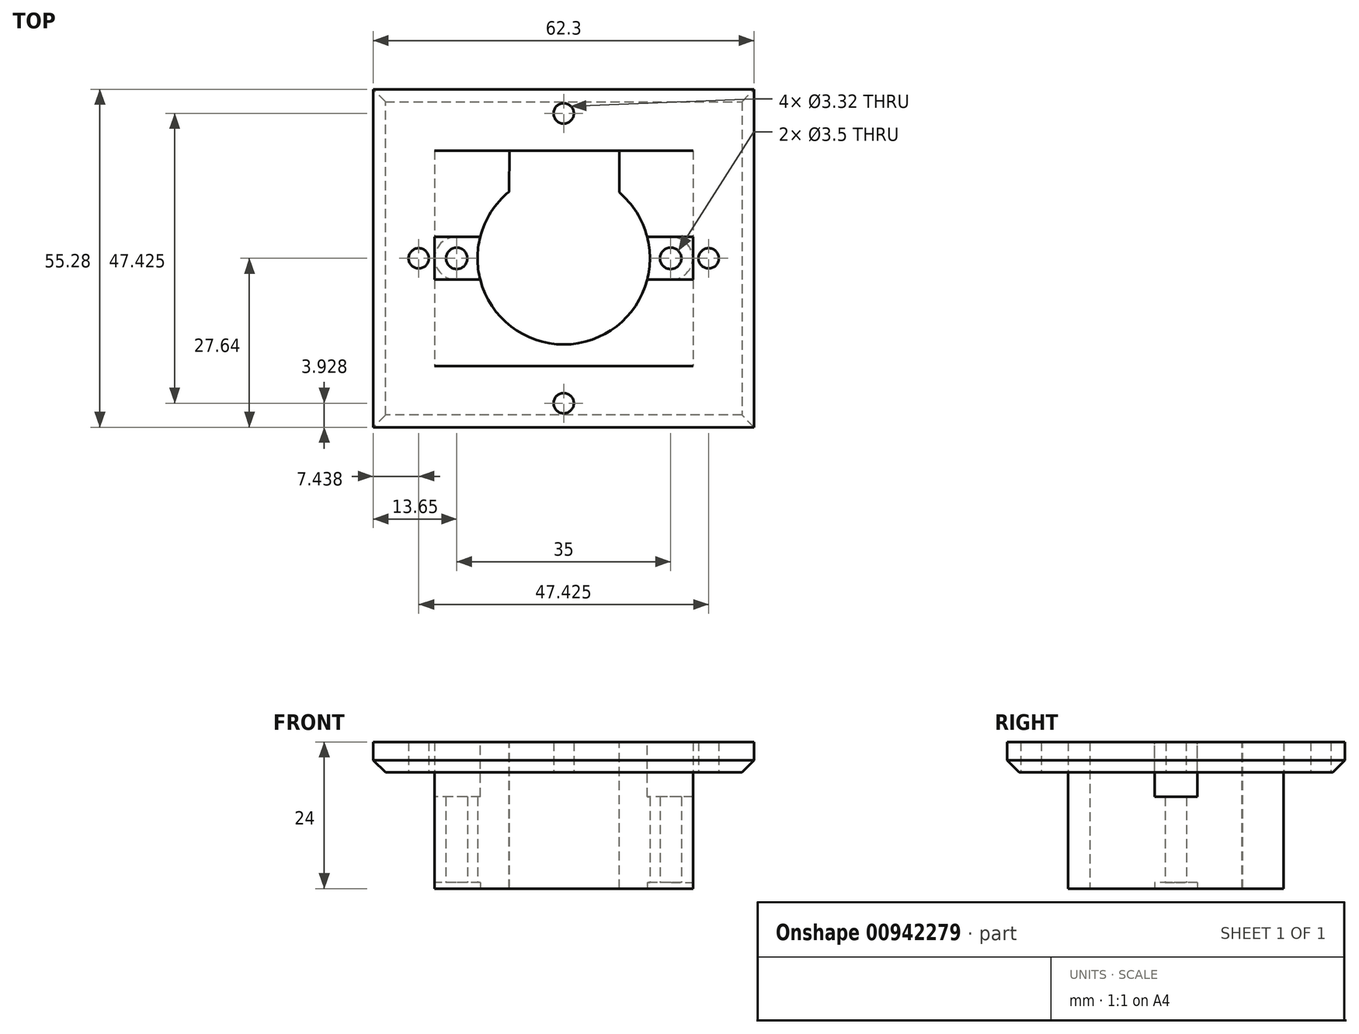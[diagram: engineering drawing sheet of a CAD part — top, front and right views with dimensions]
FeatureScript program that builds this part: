
annotation { "Feature Type Name" : "Feature", "Feature Type Description" : "" }
export const myFeature = defineFeature(function(context is Context, id is Id, definition is map)
    precondition{}
    {
        {
            var Q0;
            Q0=qCreatedBy(makeId("Top.planeOp"),FACE);
            var sketch = newSketch(context, id + "F0", { "sketchPlane" : qUnion([Q0])});
            skCircle(sketch, "E0", {"center": v(0, 0) * mm, "radius": 14.1 * mm});
            skLineSegment(sketch, "E1.bottom", {"start": v(17.6, 3.5) * mm, "end": v(13.66, 3.5) * mm});
            skLineSegment(sketch, "E1.top", {"start": v(17.6, -3.5) * mm, "end": v(13.66, -3.5) * mm});
            skLineSegment(sketch, "E1.left", {"start": v(21.1, 0) * mm, "end": v(21.1, 0) * mm});
            skLineSegment(sketch, "E1.right", {"start": v(-21.1, 0) * mm, "end": v(-21.1, 0) * mm});
            skPoint(sketch, "E2.startSnap0", {"position": v(-21.1, 0) * mm});
            skPoint(sketch, "E2.end.orphan", {"position": v(-21.1, 0) * mm});
            skPoint(sketch, "E2.start.orphan", {"position": v(-14.1, 0) * mm});
            skLineSegment(sketch, "E3.bottom", {"start": v(-17.5, 0) * mm, "end": v(-14.1, 0) * mm});
            skLineSegment(sketch, "E3.top", {"start": v(-17.5, 0) * mm, "end": v(-14.1, 0) * mm});
            skLineSegment(sketch, "E3.left", {"start": v(-17.5, 0) * mm, "end": v(-17.5, 0) * mm});
            skLineSegment(sketch, "E3.right", {"start": v(17.5, 0) * mm, "end": v(17.5, 0) * mm});
            skCircle(sketch, "E4", {"center": v(-17.5, 0) * mm, "radius": 1.75 * mm});
            skCircle(sketch, "E5", {"center": v(17.5, 0) * mm, "radius": 1.75 * mm});
            skLineSegment(sketch, "E6.bottom", {"start": v(21.15, 17.62) * mm, "end": v(-21.15, 17.62) * mm});
            skLineSegment(sketch, "E6.top", {"start": v(21.15, -17.62) * mm, "end": v(-21.15, -17.62) * mm});
            skLineSegment(sketch, "E6.left", {"start": v(21.15, 17.62) * mm, "end": v(21.15, -17.62) * mm});
            skLineSegment(sketch, "E6.right", {"start": v(-21.15, 17.62) * mm, "end": v(-21.15, -17.62) * mm});
            skLineSegment(sketch, "E7.trimOffspring", {"start": v(-13.66, 3.5) * mm, "end": v(-17.6, 3.5) * mm});
            skLineSegment(sketch, "E8.trimOffspring", {"start": v(14.1, 0) * mm, "end": v(17.5, 0) * mm});
            skLineSegment(sketch, "E9.trimOffspring", {"start": v(-13.66, -3.5) * mm, "end": v(-17.6, -3.5) * mm});
            skPoint(sketch, "E10.visualSharp", {"position": v(-21.1, 3.5) * mm});
            skArc(sketch, "E10.filletArc", {"start": v(-17.6, 3.5) * mm, "mid": v(-20.07, 2.47) * mm, "end": v(-21.1, 0) * mm});
            skPoint(sketch, "E11.visualSharp", {"position": v(-21.1, -3.5) * mm});
            skArc(sketch, "E11.filletArc", {"start": v(-21.1, 0) * mm, "mid": v(-20.07, -2.47) * mm, "end": v(-17.6, -3.5) * mm});
            skPoint(sketch, "E12.visualSharp", {"position": v(21.1, -3.5) * mm});
            skArc(sketch, "E12.filletArc", {"start": v(17.6, -3.5) * mm, "mid": v(20.07, -2.47) * mm, "end": v(21.1, 0) * mm});
            skPoint(sketch, "E13.visualSharp", {"position": v(21.1, 3.5) * mm});
            skArc(sketch, "E13.filletArc", {"start": v(21.1, 0) * mm, "mid": v(20.07, 2.47) * mm, "end": v(17.6, 3.5) * mm});
            skSolve(sketch);
        }
        {
            var Q0;
            {var subQ1=sQuery(id+"F0.wireOp",EDGE,"E1.bottom");Q0=makeQuery(id+"F0.imprint","IMPRINT",FACE,{"disambiguationData":[TD([[makeQuery(id+"F0.imprint","IMPRINT",EDGE,{"derivedFrom":subQ1}),-1.0]])]});}
            var Q1;
            {var subQ1=sQuery(id+"F0.wireOp",EDGE,"E1.top");Q1=makeQuery(id+"F0.imprint","IMPRINT",FACE,{"disambiguationData":[TD([[makeQuery(id+"F0.imprint","IMPRINT",EDGE,{"derivedFrom":subQ1}),1.0]])]});}
            var Q2;
            Q2=makeQuery(id+"F0.imprint","IMPRINT",FACE,{"disambiguationData":[TD([[makeQuery(id+"F0.imprint","IMPRINT",EDGE,{"derivedFrom":sQuery(id+"F0.wireOp",EDGE,"E4")}),-1.0]])]});
            var Q3;
            {var subQ1=sQuery(id+"F0.wireOp",EDGE,"E1.bottom");Q3=makeQuery(id+"F0.imprint","IMPRINT",FACE,{"disambiguationData":[TD([[makeQuery(id+"F0.imprint","IMPRINT",EDGE,{"derivedFrom":subQ1}),1.0]])]});}
            extrude(context, id + "F1", {"entities" : qUnion([Q0, Q1, Q2, Q3]), "depth" : 20 * mm, "offsetDistance" : 25 * mm});
        }
        {
            var Q0;
            Q0=makeQuery(id+"F1.opExtrude","CAP_FACE",FACE,{"disambiguationData":[OSD([sQuery(id+"F0.wireOp",EDGE,"E0"),sQuery(id+"F0.wireOp",EDGE,"E4"),sQuery(id+"F0.wireOp",EDGE,"E5"),sQuery(id+"F0.wireOp",EDGE,"E6.bottom"),sQuery(id+"F0.wireOp",EDGE,"E6.top"),sQuery(id+"F0.wireOp",EDGE,"E6.left"),sQuery(id+"F0.wireOp",EDGE,"E6.right")])],"isStart":false});
            var sketch = newSketch(context, id + "F2", { "sketchPlane" : qUnion([Q0])});
            skLineSegment(sketch, "E14.bottom", {"start": v(-8.89, 17.63) * mm, "end": v(9.11, 17.63) * mm});
            skLineSegment(sketch, "E14.left", {"start": v(-8.89, 17.63) * mm, "end": v(-8.93, 10.91) * mm});
            skLineSegment(sketch, "E14.right", {"start": v(9.11, 17.63) * mm, "end": v(9.07, 10.8) * mm});
            skPoint(sketch, "E14.middle", {"position": v(0, 0) * mm});
            skArc(sketch, "E15", {"start": v(9.07, 10.8) * mm, "mid": v(0.1, 14.1) * mm, "end": v(-8.93, 10.91) * mm});
            skPoint(sketch, "E14.top.end.orphan", {"position": v(8.89, -17.63) * mm});
            skPoint(sketch, "E14.top.start.orphan", {"position": v(-9.11, -17.63) * mm});
            skSolve(sketch);
        }
        {
            var Q0;
            {var subQ0=sQuery(id+"F2.wireOp",EDGE,"E15");Q0=makeQuery(id+"F2.imprint","IMPRINT",FACE,{"disambiguationData":[TD([[makeQuery(id+"F2.imprint","IMPRINT",EDGE,{"derivedFrom":subQ0}),-1.0]])]});}
            extrude(context, id + "F3", {"entities" : qUnion([Q0]), "operationType" : NewBodyOperationType.REMOVE, "oppositeDirection" : true, "depth" : 20 * mm, "offsetDistance" : 25 * mm});
        }
        {
            var Q0;
            Q0=makeQuery(id+"F0.imprint","IMPRINT",FACE,{"disambiguationData":[TD([[makeQuery(id+"F0.imprint","IMPRINT",EDGE,{"derivedFrom":sQuery(id+"F0.wireOp",EDGE,"E4")}),-1.0]])]});
            var Q1;
            {var subQ1=sQuery(id+"F0.wireOp",EDGE,"E1.bottom");Q1=makeQuery(id+"F0.imprint","IMPRINT",FACE,{"disambiguationData":[TD([[makeQuery(id+"F0.imprint","IMPRINT",EDGE,{"derivedFrom":subQ1}),1.0]])]});}
            extrude(context, id + "F4", {"entities" : qUnion([Q0, Q1]), "operationType" : NewBodyOperationType.REMOVE, "depth" : 1 * mm, "offsetDistance" : 25 * mm});
        }
        {
            var Q0;
            Q0=makeQuery(id+"F1.opExtrude","CAP_FACE",FACE,{"disambiguationData":[OSD([sQuery(id+"F0.wireOp",EDGE,"E0"),sQuery(id+"F0.wireOp",EDGE,"E4"),sQuery(id+"F0.wireOp",EDGE,"E5"),sQuery(id+"F0.wireOp",EDGE,"E6.bottom"),sQuery(id+"F0.wireOp",EDGE,"E6.top"),sQuery(id+"F0.wireOp",EDGE,"E6.left"),sQuery(id+"F0.wireOp",EDGE,"E6.right")])],"isStart":false});
            var sketch = newSketch(context, id + "F5", { "sketchPlane" : qUnion([Q0])});
            skLineSegment(sketch, "E16.bottom", {"start": v(22.67, 3.5) * mm, "end": v(-22.67, 3.5) * mm});
            skLineSegment(sketch, "E16.top", {"start": v(22.67, -3.5) * mm, "end": v(-22.67, -3.5) * mm});
            skLineSegment(sketch, "E16.left", {"start": v(22.67, 3.5) * mm, "end": v(22.67, -3.5) * mm});
            skLineSegment(sketch, "E16.right", {"start": v(-22.67, 3.5) * mm, "end": v(-22.67, -3.5) * mm});
            skPoint(sketch, "E16.middle", {"position": v(0, 0) * mm});
            skSolve(sketch);
        }
        {
            var Q0;
            Q0=makeQuery(id+"F5.imprint","IMPRINT",FACE,{"disambiguationData":[TD([[makeQuery(id+"F5.imprint","IMPRINT",EDGE,{"derivedFrom":makeQuery(id+"F1.opExtrude","CAP_EDGE",EDGE,{"disambiguationData":[OSD([sQuery(id+"F0.wireOp",EDGE,"E4")])],"isStart":false})}),-1.0]])]});
            var Q1;
            Q1=makeQuery(id+"F5.imprint","IMPRINT",FACE,{"disambiguationData":[TD([[makeQuery(id+"F5.imprint","IMPRINT",EDGE,{"derivedFrom":makeQuery(id+"F1.opExtrude","CAP_EDGE",EDGE,{"disambiguationData":[OSD([sQuery(id+"F0.wireOp",EDGE,"E5")])],"isStart":false})}),-1.0]])]});
            extrude(context, id + "F6", {"entities" : qUnion([Q0, Q1]), "operationType" : NewBodyOperationType.REMOVE, "oppositeDirection" : true, "depth" : 5 * mm, "offsetDistance" : 25 * mm});
        }
        {
            var Q0;
            {var subQ0=sQuery(id+"F0.wireOp",EDGE,"E6.bottom");var subQ1=sQuery(id+"F0.wireOp",EDGE,"E6.right");var subQ2=sQuery(id+"F0.wireOp",EDGE,"E0");Q0=makeQuery(id+"F6.boolean.opBoolean","SPLIT",FACE,{"disambiguationData":[TD([makeQuery(id+"F3.boolean.opBoolean","COPY",FACE,{"derivedFrom":makeQuery(id+"F3.opExtrude","SWEPT_FACE",FACE,{"disambiguationData":[OSD([sQuery(id+"F2.wireOp",EDGE,"E14.left")])]})})])],"derivedFrom":makeQuery(id+"F1.opExtrude","CAP_FACE",FACE,{"disambiguationData":[OSD([subQ2,sQuery(id+"F0.wireOp",EDGE,"E4"),sQuery(id+"F0.wireOp",EDGE,"E5"),subQ0,sQuery(id+"F0.wireOp",EDGE,"E6.top"),sQuery(id+"F0.wireOp",EDGE,"E6.left"),subQ1])],"isStart":false})});}
            var sketch = newSketch(context, id + "F7", { "sketchPlane" : qUnion([Q0])});
            skLineSegment(sketch, "E17.bottom", {"start": v(21.15, 17.64) * mm, "end": v(-21.15, 17.64) * mm});
            skLineSegment(sketch, "E17.top", {"start": v(21.15, -17.64) * mm, "end": v(-21.15, -17.64) * mm});
            skLineSegment(sketch, "E17.left", {"start": v(21.15, 17.64) * mm, "end": v(21.15, -17.64) * mm});
            skLineSegment(sketch, "E17.right", {"start": v(-21.15, 17.64) * mm, "end": v(-21.15, -17.64) * mm});
            skPoint(sketch, "E17.middle", {"position": v(0, 0) * mm});
            skLineSegment(sketch, "E18.0", {"start": v(31.15, 27.64) * mm, "end": v(-31.15, 27.64) * mm});
            skLineSegment(sketch, "E18.1", {"start": v(31.15, 27.64) * mm, "end": v(31.15, -27.64) * mm});
            skLineSegment(sketch, "E18.2", {"start": v(31.15, -27.64) * mm, "end": v(-31.15, -27.64) * mm});
            skLineSegment(sketch, "E18.3", {"start": v(-31.15, 27.64) * mm, "end": v(-31.15, -27.64) * mm});
            skSolve(sketch);
        }
        {
            var Q0;
            {var subQ5=sQuery(id+"F7.wireOp",EDGE,"E17.bottom");Q0=makeQuery(id+"F7.imprint","IMPRINT",FACE,{"disambiguationData":[TD([[makeQuery(id+"F7.imprint","IMPRINT",EDGE,{"derivedFrom":subQ5}),-1.0]])]});}
            extrude(context, id + "F8", {"entities" : qUnion([Q0]), "depth" : 4 * mm, "offsetDistance" : 25 * mm});
        }
        {
            var Q0;
            Q0=makeQuery(id+"F8.opExtrude","CAP_FACE",FACE,{"disambiguationData":[OSD([sQuery(id+"F7.wireOp",EDGE,"E17.bottom"),sQuery(id+"F7.wireOp",EDGE,"E17.top"),sQuery(id+"F7.wireOp",EDGE,"E17.left"),sQuery(id+"F7.wireOp",EDGE,"E17.right"),sQuery(id+"F7.wireOp",EDGE,"E18.0"),sQuery(id+"F7.wireOp",EDGE,"E18.1"),sQuery(id+"F7.wireOp",EDGE,"E18.2"),sQuery(id+"F7.wireOp",EDGE,"E18.3")])],"isStart":true});
            extrude(context, id + "F9", {"entities" : qUnion([Q0]), "depth" : 1 * mm, "offsetDistance" : 25 * mm});
        }
        {
            var Q0;
            {var subQ0=sQuery(id+"F0.wireOp",EDGE,"E6.bottom");var subQ1=sQuery(id+"F0.wireOp",EDGE,"E6.right");var subQ2=sQuery(id+"F0.wireOp",EDGE,"E0");Q0=makeQuery(id+"F6.boolean.opBoolean","SPLIT",FACE,{"disambiguationData":[TD([makeQuery(id+"F3.boolean.opBoolean","COPY",FACE,{"derivedFrom":makeQuery(id+"F3.opExtrude","SWEPT_FACE",FACE,{"disambiguationData":[OSD([sQuery(id+"F2.wireOp",EDGE,"E14.left")])]})})])],"derivedFrom":makeQuery(id+"F1.opExtrude","CAP_FACE",FACE,{"disambiguationData":[OSD([subQ2,sQuery(id+"F0.wireOp",EDGE,"E4"),sQuery(id+"F0.wireOp",EDGE,"E5"),subQ0,sQuery(id+"F0.wireOp",EDGE,"E6.top"),sQuery(id+"F0.wireOp",EDGE,"E6.left"),subQ1])],"isStart":false})});}
            var Q1;
            {var subQ0=sQuery(id+"F0.wireOp",EDGE,"E6.left");var subQ1=sQuery(id+"F0.wireOp",EDGE,"E6.bottom");var subQ2=sQuery(id+"F0.wireOp",EDGE,"E0");Q1=makeQuery(id+"F6.boolean.opBoolean","SPLIT",FACE,{"disambiguationData":[TD([makeQuery(id+"F3.boolean.opBoolean","COPY",FACE,{"derivedFrom":makeQuery(id+"F3.opExtrude","SWEPT_FACE",FACE,{"disambiguationData":[OSD([sQuery(id+"F2.wireOp",EDGE,"E14.right")])]})})])],"derivedFrom":makeQuery(id+"F1.opExtrude","CAP_FACE",FACE,{"disambiguationData":[OSD([subQ2,sQuery(id+"F0.wireOp",EDGE,"E4"),sQuery(id+"F0.wireOp",EDGE,"E5"),subQ1,sQuery(id+"F0.wireOp",EDGE,"E6.top"),subQ0,sQuery(id+"F0.wireOp",EDGE,"E6.right")])],"isStart":false})});}
            var Q2;
            {var subQ0=sQuery(id+"F0.wireOp",EDGE,"E6.right");var subQ1=sQuery(id+"F0.wireOp",EDGE,"E6.left");var subQ2=sQuery(id+"F0.wireOp",EDGE,"E6.top");var subQ3=sQuery(id+"F0.wireOp",EDGE,"E0");Q2=makeQuery(id+"F6.boolean.opBoolean","SPLIT",FACE,{"disambiguationData":[TD([makeQuery(id+"F1.opExtrude","SWEPT_FACE",FACE,{"disambiguationData":[OSD([subQ2])]})])],"derivedFrom":makeQuery(id+"F1.opExtrude","CAP_FACE",FACE,{"disambiguationData":[OSD([subQ3,sQuery(id+"F0.wireOp",EDGE,"E4"),sQuery(id+"F0.wireOp",EDGE,"E5"),sQuery(id+"F0.wireOp",EDGE,"E6.bottom"),subQ2,subQ1,subQ0])],"isStart":false})});}
            extrude(context, id + "F10", {"entities" : qUnion([Q0, Q1, Q2]), "operationType" : NewBodyOperationType.ADD, "depth" : 4 * mm, "offsetDistance" : 25 * mm});
        }
        {
            var Q0;
            Q0=makeQuery(id+"F9.opExtrude","CAP_FACE",FACE,{"disambiguationData":[OSD([sQuery(id+"F7.wireOp",EDGE,"E17.bottom"),sQuery(id+"F7.wireOp",EDGE,"E17.top"),sQuery(id+"F7.wireOp",EDGE,"E17.left"),sQuery(id+"F7.wireOp",EDGE,"E17.right"),sQuery(id+"F7.wireOp",EDGE,"E18.0"),sQuery(id+"F7.wireOp",EDGE,"E18.1"),sQuery(id+"F7.wireOp",EDGE,"E18.2"),sQuery(id+"F7.wireOp",EDGE,"E18.3")])],"isStart":false});
            var sketch = newSketch(context, id + "F11", { "sketchPlane" : qUnion([Q0])});
            skLineSegment(sketch, "E19.bottom", {"start": v(31.15, 27.64) * mm, "end": v(-31.15, 27.64) * mm});
            skLineSegment(sketch, "E19.top", {"start": v(31.15, -27.64) * mm, "end": v(-31.15, -27.64) * mm});
            skLineSegment(sketch, "E19.left", {"start": v(31.15, 27.64) * mm, "end": v(31.15, -27.64) * mm});
            skLineSegment(sketch, "E19.right", {"start": v(-31.15, 27.64) * mm, "end": v(-31.15, -27.64) * mm});
            skPoint(sketch, "E19.middle", {"position": v(0, 0) * mm});
            skCircle(sketch, "E20", {"center": v(0, 23.71) * mm, "radius": 1.66 * mm});
            skCircle(sketch, "E21.1.0", {"center": v(-23.71, 0) * mm, "radius": 1.66 * mm});
            skCircle(sketch, "E21.2.0", {"center": v(0, -23.71) * mm, "radius": 1.66 * mm});
            skCircle(sketch, "E22.1.3.0", {"center": v(23.71, 0) * mm, "radius": 1.66 * mm});
            skSolve(sketch);
        }
        {
            var Q0;
            Q0=makeQuery(id+"F11.imprint","IMPRINT",FACE,{"disambiguationData":[TD([[makeQuery(id+"F11.imprint","IMPRINT",EDGE,{"derivedFrom":sQuery(id+"F11.wireOp",EDGE,"E20")}),1.0]])]});
            var Q1;
            Q1=makeQuery(id+"F11.imprint","IMPRINT",FACE,{"disambiguationData":[TD([[makeQuery(id+"F11.imprint","IMPRINT",EDGE,{"derivedFrom":sQuery(id+"F11.wireOp",EDGE,"E22.1.3.0")}),1.0]])]});
            var Q2;
            Q2=makeQuery(id+"F11.imprint","IMPRINT",FACE,{"disambiguationData":[TD([[makeQuery(id+"F11.imprint","IMPRINT",EDGE,{"derivedFrom":sQuery(id+"F11.wireOp",EDGE,"E21.2.0")}),1.0]])]});
            var Q3;
            Q3=makeQuery(id+"F11.imprint","IMPRINT",FACE,{"disambiguationData":[TD([[makeQuery(id+"F11.imprint","IMPRINT",EDGE,{"derivedFrom":sQuery(id+"F11.wireOp",EDGE,"E21.1.0")}),1.0]])]});
            extrude(context, id + "F12", {"entities" : qUnion([Q0, Q1, Q2, Q3]), "operationType" : NewBodyOperationType.REMOVE, "oppositeDirection" : true, "depth" : 6 * mm, "offsetDistance" : 25 * mm});
        }
        {
            var Q0;
            Q0=makeQuery(id+"F9.opExtrude","CAP_EDGE",EDGE,{"disambiguationData":[OSD([sQuery(id+"F7.wireOp",EDGE,"E18.3")])],"isStart":false});
            var Q1;
            Q1=makeQuery(id+"F9.opExtrude","CAP_EDGE",EDGE,{"disambiguationData":[OSD([sQuery(id+"F7.wireOp",EDGE,"E18.2")])],"isStart":false});
            var Q2;
            Q2=makeQuery(id+"F9.opExtrude","CAP_EDGE",EDGE,{"disambiguationData":[OSD([sQuery(id+"F7.wireOp",EDGE,"E18.1")])],"isStart":false});
            var Q3;
            Q3=makeQuery(id+"F9.opExtrude","CAP_EDGE",EDGE,{"disambiguationData":[OSD([sQuery(id+"F7.wireOp",EDGE,"E18.0")])],"isStart":false});
            chamfer(context, id + "F13", {"entities" : qUnion([Q0, Q1, Q2, Q3]), "width" : 2 * mm, "tangentPropagation" : true});
        }
    });
